# Revit family: Faucet_Touchless-Lavatory-KOHLER-Sculpted-K-13462_1
name_source: partatom
category: Plumbing Fixtures
units: mm (PartAtom-declared; Revit-internal decimal feet)

## family parameters
Cut with Voids When Loaded = No
Host = Face
OmniClass Number = 23.31.11.00
OmniClass Title = Faucets
Part Type = Normal
Room Calculation Point = No
Round Connector Dimension = Use Diameter
Shared = No

## types (3) — shared parameters
Apparent Load = 0 VA
Assembly Code = D2010
CW Connection = Yes
Cold Water Inlet = Cold Water Inlet
Date Modified = 04/17/2023
Default Elevation = 36"
Drain Included = No
Electrical Connector = Yes
Electrical Note = One Dedicated Circuite Requiered
Faucet Hole Spacing = 0"
HW Connection = Yes
Handle Clearance = 0"
Height = 5 13/16"
Hot Water Inlet = Hot Water Inlet
Length = 5"
Manufacturer = Kohler Co.
Master Format 2014 = 22 41 39
Master Format 2014 Name = Residential Faucets, Supplies, and Trim
Material = Premium Metal Construction
Pressure = 0.00 psi
Product Documentation Link = https://www.us.kohler.com
Product Name = Sculpted
Product Page URL = http://www.us.kohler.com
Spout Reach = 5"
URL = https://www.us.kohler.com
Vent Connection = No
Voltage = 120 V
Waste Connection = No
Waste Water Outlet = Waste Water Outlet
WaterSense Certified = No
Width = 2 5/8"

## per-type parameters (varying)
| type | ADA Compliant | Description | Finish | Flow Rate | Model | Type |
| 0.5GPM, CP-Polished Chrome | Yes | Touchless single-hole lavatory sink faucet with Insight sensor technology and temperature mixer, AC-powered, 0.5 gpm | Kohler-Metal-CP-Polished_Chrome | 1 GPM | K-13462-CP | 2 |
| 0.5GPM, VS-Vibrant Stainless | Yes | Touchless single-hole lavatory sink faucet with Insight sensor technology and temperature mixer, AC-powered, 0.5 gpm | Kohler-Metal-VS-Vibrant_Stainless | 1 GPM | K-13462-VS | 3 |
| 0.35GPM, CP-Polished Chrome | No | INSIGHT AC MIXER 0.35GPM | Kohler-Metal-CP-Polished_Chrome | 0 GPM | K-13462-SATA-CP | 1 |

## geometry (parser evidence)
native form markers: Sweep x5
no freeform markers — native parametric forms only
